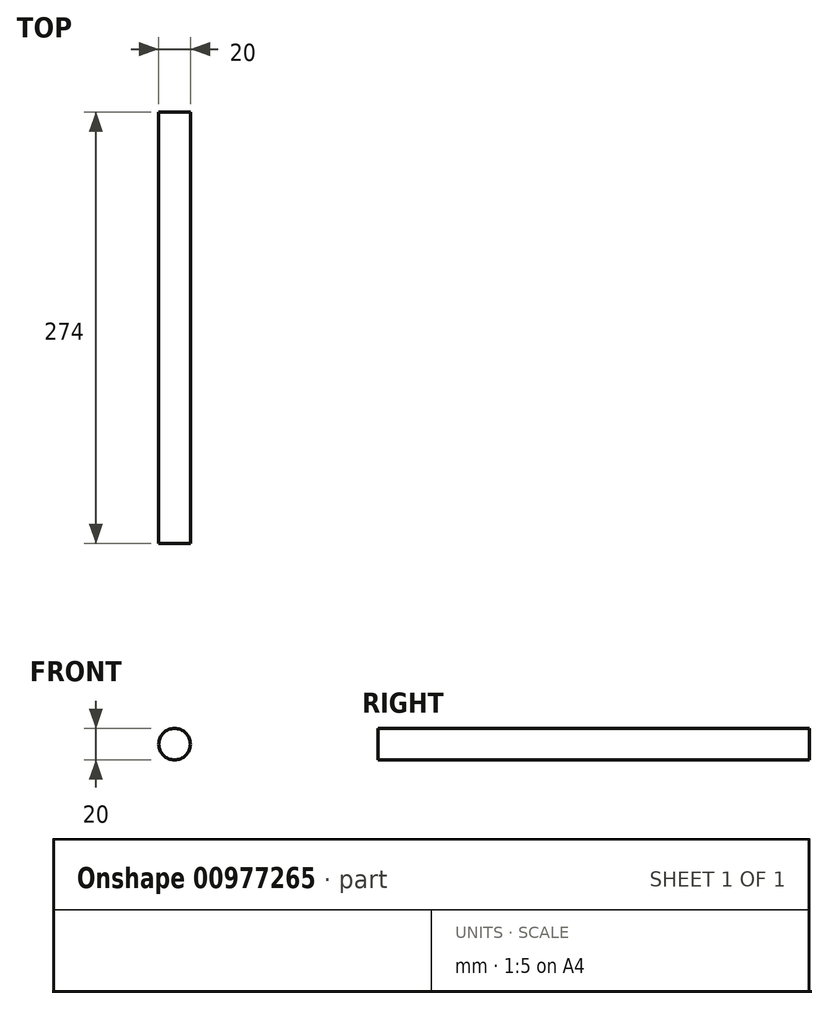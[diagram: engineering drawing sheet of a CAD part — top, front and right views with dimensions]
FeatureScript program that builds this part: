
annotation { "Feature Type Name" : "Feature", "Feature Type Description" : "" }
export const myFeature = defineFeature(function(context is Context, id is Id, definition is map)
    precondition{}
    {
        {
            var Q0;
            Q0=qCreatedBy(makeId("Front.planeOp"),FACE);
            var sketch = newSketch(context, id + "F0", { "sketchPlane" : qUnion([Q0])});
            skCircle(sketch, "E0", {"center": v(0, 0) * mm, "radius": 10 * mm});
            skSolve(sketch);
        }
        {
            var Q0;
            Q0=qSketchRegion(id+"F0",true);
            extrude(context, id + "F1", {"entities" : qUnion([Q0]), "depth" : 274 * mm, "offsetDistance" : 25 * mm, "symmetric" : true});
        }
    });
